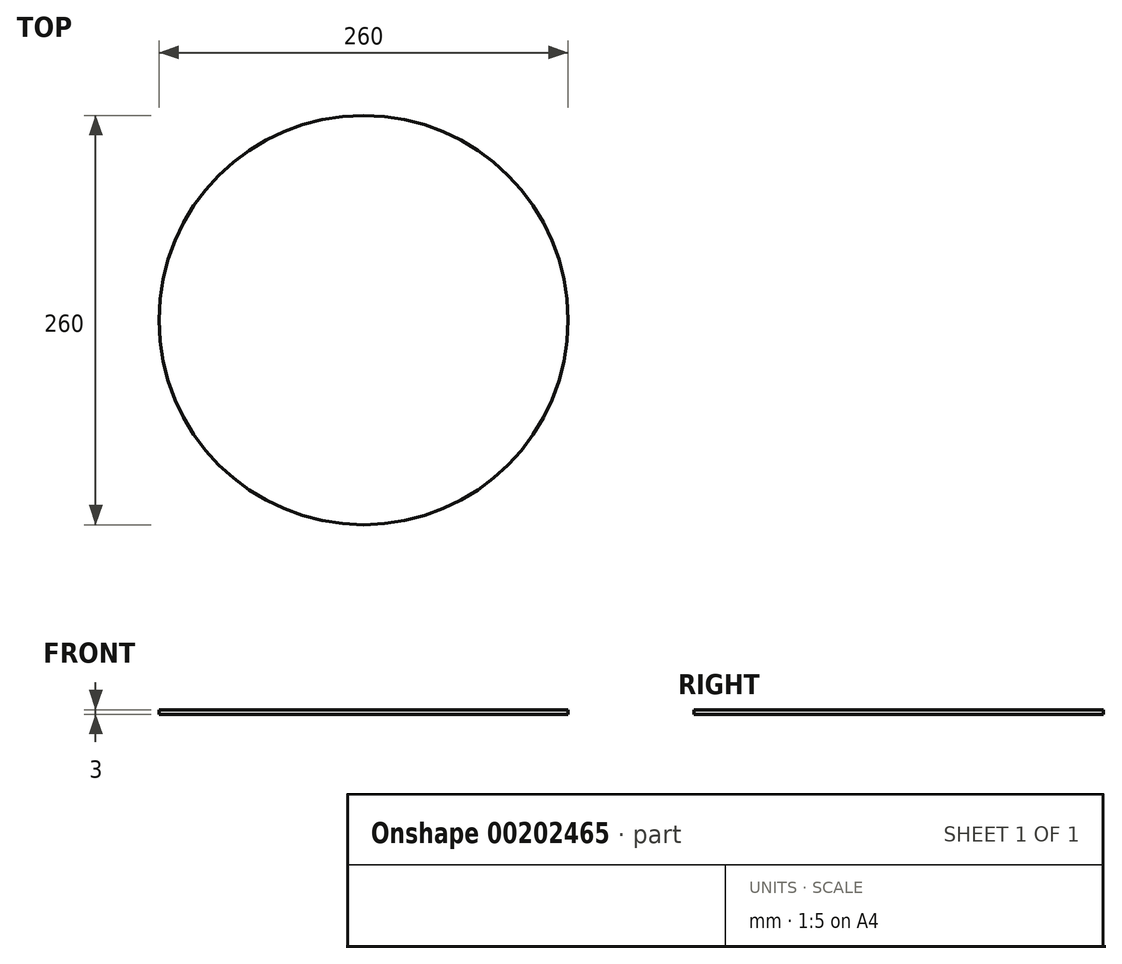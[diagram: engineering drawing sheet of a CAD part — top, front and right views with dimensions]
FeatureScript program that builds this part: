
annotation { "Feature Type Name" : "Feature", "Feature Type Description" : "" }
export const myFeature = defineFeature(function(context is Context, id is Id, definition is map)
    precondition{}
    {
        {
            var Q0;
            Q0=qCreatedBy(makeId("Top.planeOp"),FACE);
            var sketch = newSketch(context, id + "F0", { "sketchPlane" : qUnion([Q0])});
            skCircle(sketch, "E0", {"center": v(0, 0) * mm, "radius": 130 * mm});
            skSolve(sketch);
        }
        {
            var Q0;
            Q0=qSketchRegion(id+"F0",true);
            extrude(context, id + "F1", {"entities" : qUnion([Q0]), "depth" : 3 * mm});
        }
    });
